# Revit family: Franke_Tassenwärmer_A-Serie-A600_A800_A1000
name_source: partatom
category: Sonderausstattung
revit_build: Autodesk Revit 2015 (Build: 20140606_1530(x64)
units: mm (PartAtom-declared; Revit-internal decimal feet)

## types (2) — shared parameters
Ablagekapazität = 120 Tassen
Anzahl der Nullleiter = 1
Anzahl der Schutzleiter = 1
Anzahl von Polen = 1
Aufstellgewicht = 20 kg
Bauelement = Beistellgerät Tassenwärmer
Baugruppenkennzeichen = Beistellgerät Tassenwärmer
Beschreibung = Beistellgerät Tassenwärmer dient zur Vorwärmung und Bereitstellung von Tassen, Untertassen und Gläsern
Breite = 270 mm  [stored 0.885827 ft]
Energieverlust nach DIN18873 = k.A.
Hersteller = Franke
Höhe = 585 mm  [stored 1.91929 ft]
Leistung max. = 130 W
Leistung min. = 110 W
Modell = 410894 - Tassenwärmer A-Serie - A600, A800, A1000
Netzfrequenz = 50 Hz
Netzfrequenz alternativ = 60 Hz
Sicherung = 10 A
Spannung = 230 V
Tiefe = 453 mm  [stored 1.48622 ft]
URL = http://www.franke.com
zero-valued in all types: Kosten

## per-type parameters (varying)
| type | Abdeckung |
| Tassenwärmer A-Serie-A600,A800,A1000(230V/black line/EU) | Franke Black |
| Tassenwärmer A-Serie-A600,A800,A1000(230V/anthrazit/EU) | Franke Anthrazit |

note: [stored X ft] marks values corroborated as IEEE doubles in the binary element streams (Revit-internal decimal feet)
